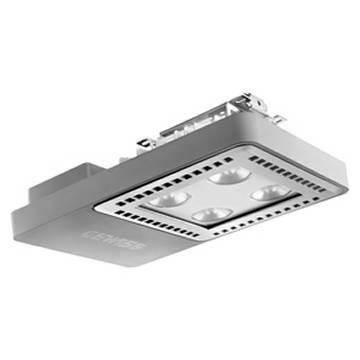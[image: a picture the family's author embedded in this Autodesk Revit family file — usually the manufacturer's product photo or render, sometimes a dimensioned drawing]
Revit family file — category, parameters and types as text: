
# Revit family: Lighting-Industrial-GEWISS-SMART[4]HLO_HIGHBAYS-LED_EMERGENCY_1M
name_source: partatom
category: Apparecchi per illuminazione
units: mm (PartAtom-declared; Revit-internal decimal feet)

## family parameters
Basato su piano di lavoro = Sì
Condiviso = No
Numero OmniClass = 23.80.00.00
Punto di calcolo locali = No
Quota connettore circolare = Usa diametro
Sempre verticale = No
Sorgente d'illuminazione = No
Taglio con vuoti quando caricato = No
Tipo di parte = Normale
Titolo OmniClass = Electric Power and Lighting

## types (18) — shared parameters
Application = Internal
Body = PA6 "Halogen Free" loaded fibreglass
Carico apparente = 50 VA
Catalogue = LIGHTING
Classification: = -
Classificazione = Lighting
Color Rendering Index = CRI-80
Colour = Grey RAL 7035
Colour : = Grey RAL 7035
Commenti sul wattaggio = 50W
Context = Logistics and industrial manufacturing lighting
Control System = 1 x DALI DT6 + 1 x DALI DT1 (Emerg. 3h)
DIN 18032-3 certification = -
Device with reduced surface temperature = Yes
Distanza tot_plafoniera = 74 mm  [stored 0.242782 ft]
Driver = Included
Driver Box = Built-in
Electrocod = 2444
Eletrical and lighting features = -
External screw = Stainless steel
Fixing = -
Gasket = anti-aging silicone
General information = -
Glow Wire Test : = 850 °C
IDF = c2843a42-114d-4628-8d4d-b7f9c19c0e6a
IDT = dbfa2a0d0d304b5c9c716a8a975efb61
IP degree = IP65
IPEA = -
Immagine tipo = GWL1071.jpg
Installationa and maintenance = -
Insulation class = I
LED Maintenance = NiMh Battery Only
Lampada = LED
Larghezza = 253 mm  [stored 0.830052 ft]
Lifetime = L90B10 (Tq+25°C) = 100.000 h - L90B10 (Tq+50°C) = 50.000 h
Locking Hook = -
Luminaire = LED Industrial ReflectorÂ
Lunghezza = 383 mm  [stored 1.25656 ft]
Materials = -
Maximum surface exposed to the wind : = 0,140 m²
Motore = <Per categoria>
Mouting and installation = Ceiling light - Suspension
Operating temperature : = 0 ÷ +40 °C
Optic Maintenance = Non-replaceable
Optic and illuminating features = -
Overvoltage protection = DM 6 kV / CM 10 kV
Photobiological Risk Class = RG0
Plafoniera = <Per categoria>
Produttore = GEWISS S.p.A.
Prospetto di default = 1219 mm
Raggio led = 30 mm  [stored 0.0984252 ft]
Rated frequency (Hz) = 50/60 Hz
Shield type = Tempered glass Thickness 4mm
Shock resistance = IK08
Spessore plafoniera = 40 mm  [stored 0.131234 ft]
Standard Deviation Colour Matching = SDCM = 3
Standard- = EN 60598-2-22 ; EN 60598-1 ; EN 60598-2-24
Standards and approvals = -
Stocking temperature = -40 +70 °C
Supply voltage = 220 - 240 V
System power : = 64 W (+5W Emerg.)
Technical sheet = https://www.gewiss.com
Tilt- = -
Trasformatore = <Per categoria>
Type of light source = LED - Not replaceable
URL = https://www.gewiss.com
Unique digital code (Datamatrix) = Datamatrix
Version file RFA = 20.11
Vetro acceso = Lampada accesa
Voltaggio = 230 V
Warranty = 5 years
Weight (kg): = 5
Wiring = With GW connect watertight connector

## per-type parameters (varying)
| type | Colour temperature | Descrizione | Efficiency (lm/W) | Lumen output (lm) : | Modello | Optic | Optic : | Unified Glare Rating |
| GWS4124BF830 - SMART4LB 1M EMERG.HLO 30° 30K | 3000K | SMART[4]LB 1M EMERG.HLO 30° 30K | 125 | 8600 (810 Emerg.) | GWS4124BF830 | 30° | Metallic PC reflector and PMMA lenses | UGR - 22 |
| GWS4124BP857 - SMART4LB 1M EMERG.HLO 90° 57K | 5700K | SMART[4]LB 1M EMERG.HLO 90° 57K | 133 | 9200 (850 Emerg.) | GWS4124BP857 | 90° | Metallic PC reflector and PMMA lenses | UGR - 25 |
| GWS4124BF840 - SMART4LB 1M EMERG.HLO 30° 40K | 4000K | SMART[4]LB 1M EMERG.HLO 30° 40K | 130 | 9000 (850 Emerg.) | GWS4124BF840 | 30° | Metallic PC reflector and PMMA lenses | UGR - 22 |
| GWS4124BC840 - SMART4LB 1M EMERG.HLO ASI.40K | 4000K | SMART[4]LB 1M EMERG.HLO ASI.40K | 119 | 8200 (750 Emerg.) | GWS4124BC840 | Asymmetrical | Metallic PC reflector and PMMA lenses | - |
| GWS4124BF857 - SMART4LB 1M EMERG.HLO 30° 57K | 5700K | SMART[4]LB 1M EMERG.HLO 30° 57K | 130 | 9000 (850 Emerg.) | GWS4124BF857 | 30° | Metallic PC reflector and PMMA lenses | UGR - 22 |
| GWS4124BQ840 - SMART4LB 1M EMERG.HLO ELL.40K | 4000K | SMART[4]LB 1M EMERG.HLO ELL.40K | 119 | 8200 (750 Emerg.) | GWS4124BQ840 | Elliptical | Metallic PC reflector and PMMA lenses | - |
| GWS4124BA840 - SMART4LB 1M EMERG.HLO ARR.40K | 4000K | SMART[4]LB 1M EMERG.HLO ARR.40K | 133 | 9200 (850 Emerg.) | GWS4124BA840 | Array | Metallized polycarbonate reflector | - |
| GWS4124BC830 - SMART4LB 1M EMERG.HLO ASI.30K | 3000K | SMART[4]LB 1M EMERG.HLO ASI.30K | 113 | 7800 (710 Emerg.) | GWS4124BC830 | Asymmetrical | Metallic PC reflector and PMMA lenses | - |
| GWS4124BQ830 - SMART4LB 1M EMERG.HLO ELL.30K | 3000K | SMART[4]LB 1M EMERG.HLO ELL.30K | 113 | 7800 (710 Emerg.) | GWS4124BQ830 | Elliptical | Metallic PC reflector and PMMA lenses | - |
| GWS4124BA830 - SMART4LB 1M EMERG.HLO ARR.30K | 3000K | SMART[4]LB 1M EMERG.HLO ARR.30K | 126 | 8700 (810 Emerg.) | GWS4124BA830 | Array | Metallized polycarbonate reflector | - |
| GWS4124BP840 - SMART4LB 1M EMERG.HLO 90° 40K | 4000K | SMART[4]LB 1M EMERG.HLO 90° 40K | 133 | 9200 (850 Emerg.) | GWS4124BP840 | 90° | Metallic PC reflector and PMMA lenses | UGR - 25 |
| GWS4124BC857 - SMART4LB 1M EMERG.HLO ASI.57K | 5700K | SMART[4]LB 1M EMERG.HLO ASI.57K | 119 | 8200 (750 Emerg.) | GWS4124BC857 | Asymmetrical | Metallic PC reflector and PMMA lenses | - |
| GWS4124BH857 - SMART4LB 1M EMERG.HLO 60° 57K | 5700K | SMART[4]LB 1M EMERG.HLO 60° 57K | 133 | 9200 (850 Emerg.) | GWS4124BH857 | 60° | Metallic PC reflector and PMMA lenses | UGR - 25 |
| GWS4124BH830 - SMART4LB 1M EMERG.HLO 60° 30K | 3000K | SMART[4]LB 1M EMERG.HLO 60° 30K | 126 | 8700 (810 Emerg.) | GWS4124BH830 | 60° | Metallic PC reflector and PMMA lenses | UGR - 25 |
| GWS4124BQ857 - SMART4LB 1M EMERG.HLO ELL.57K | 5700K | SMART[4]LB 1M EMERG.HLO ELL.57K | 119 | 8200 (750 Emerg.) | GWS4124BQ857 | Elliptical | Metallic PC reflector and PMMA lenses | - |
| GWS4124BP830 - SMART4LB 1M EMERG.HLO 90° 30K | 3000K | SMART[4]LB 1M EMERG.HLO 90° 30K | 128 | 8800 (810 Emerg.) | GWS4124BP830 | 90° | Metallic PC reflector and PMMA lenses | UGR - 25 |
| GWS4124BH840 - SMART4LB 1M EMERG.HLO 60° 40K | 4000K | SMART[4]LB 1M EMERG.HLO 60° 40K | 133 | 9200 (850 Emerg.) | GWS4124BH840 | 60° | Metallic PC reflector and PMMA lenses | UGR - 25 |
| GWS4124BA857 - SMART4LB 1M EMERG.HLO ARR.57K | 5700K | SMART[4]LB 1M EMERG.HLO ARR.57K | 133 | 9200 (850 Emerg.) | GWS4124BA857 | Array | Metallized polycarbonate reflector | - |

note: [stored X ft] marks values corroborated as IEEE doubles in the binary element streams (Revit-internal decimal feet)

## geometry (parser evidence)
native form markers: Blend x4
no freeform markers — native parametric forms only
